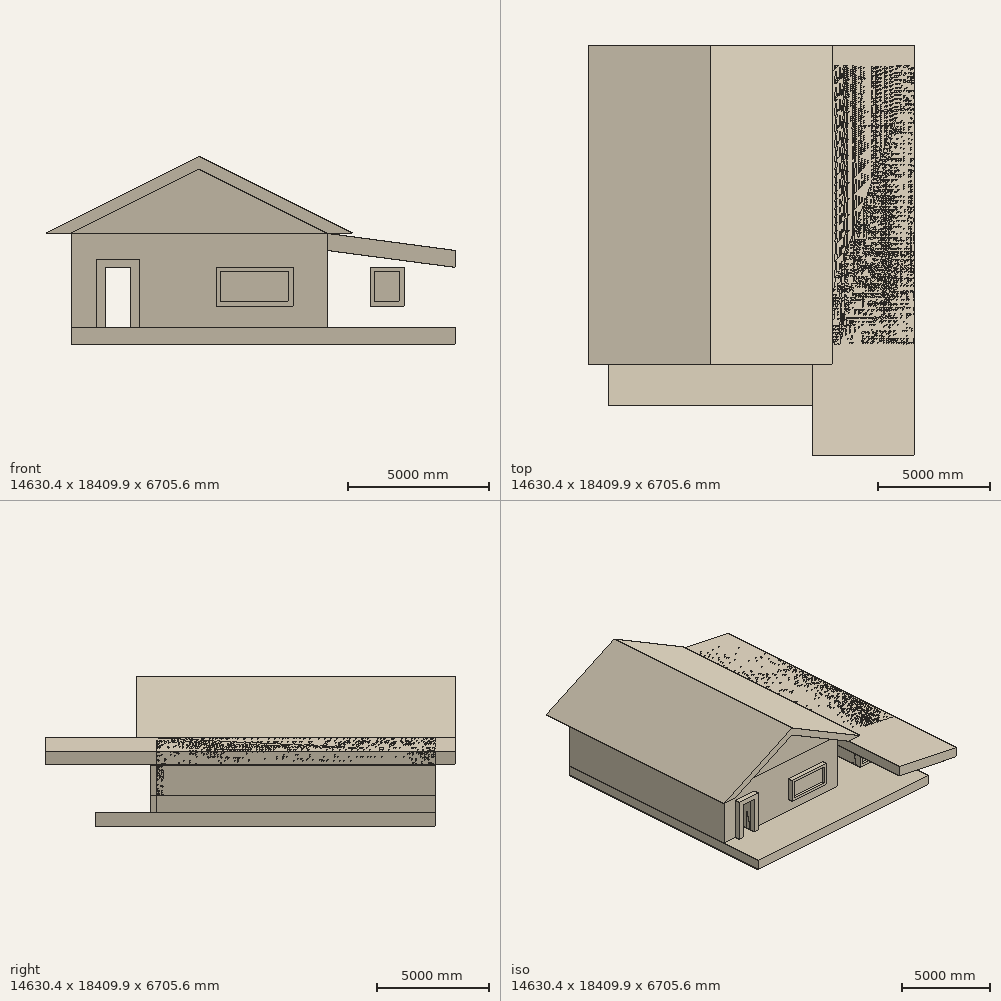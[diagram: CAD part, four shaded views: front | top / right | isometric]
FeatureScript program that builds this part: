
annotation { "Feature Type Name" : "Feature", "Feature Type Description" : "" }
export const myFeature = defineFeature(function(context is Context, id is Id, definition is map)
    precondition{}
    {
        {
            var Q0;
            Q0=qCreatedBy(makeId("Front.planeOp"),FACE);
            var sketch = newSketch(context, id + "F0", { "sketchPlane" : qUnion([Q0])});
            skLineSegment(sketch, "E0", {"start": v(0, 0) * mm, "end": v(-4572, 0) * mm});
            skLineSegment(sketch, "E1", {"start": v(0, 0) * mm, "end": v(4572, 0) * mm});
            skLineSegment(sketch, "E2", {"start": v(0, 0) * mm, "end": v(0, 2286) * mm});
            skLineSegment(sketch, "E3", {"start": v(0, 2286) * mm, "end": v(-4572, 0) * mm});
            skLineSegment(sketch, "E4", {"start": v(0, 2286) * mm, "end": v(4572, 0) * mm});
            skLineSegment(sketch, "E5", {"start": v(-4572, 0) * mm, "end": v(-5486.4, 0) * mm});
            skLineSegment(sketch, "E6", {"start": v(0, 2286) * mm, "end": v(0, 2743.2) * mm});
            skLineSegment(sketch, "E7", {"start": v(0, 2743.2) * mm, "end": v(-5486.4, 0) * mm});
            skLineSegment(sketch, "E8", {"start": v(4572, 0) * mm, "end": v(5486.4, 0) * mm});
            skLineSegment(sketch, "E9", {"start": v(5486.4, 0) * mm, "end": v(0, 2743.2) * mm});
            skLineSegment(sketch, "E10", {"start": v(-4572, 0) * mm, "end": v(-4572, -3352.8) * mm});
            skLineSegment(sketch, "E11", {"start": v(-4572, -3352.8) * mm, "end": v(4572, -3352.8) * mm});
            skLineSegment(sketch, "E12", {"start": v(4572, -3352.8) * mm, "end": v(4572, 0) * mm});
            skLineSegment(sketch, "E13", {"start": v(-4572, -3352.8) * mm, "end": v(-4572, -3962.4) * mm});
            skLineSegment(sketch, "E14", {"start": v(-4572, -3962.4) * mm, "end": v(4572, -3962.4) * mm});
            skLineSegment(sketch, "E15", {"start": v(4572, -3962.4) * mm, "end": v(4572, -3352.8) * mm});
            skLineSegment(sketch, "E16.bottom", {"start": v(-3352.8, -3352.8) * mm, "end": v(-2438.4, -3352.8) * mm});
            skLineSegment(sketch, "E16.top", {"start": v(-3352.8, -1219.2) * mm, "end": v(-2438.4, -1219.2) * mm});
            skLineSegment(sketch, "E16.left", {"start": v(-3352.8, -3352.8) * mm, "end": v(-3352.8, -1219.2) * mm});
            skLineSegment(sketch, "E16.right", {"start": v(-2438.4, -3352.8) * mm, "end": v(-2438.4, -1219.2) * mm});
            skLineSegment(sketch, "E17.bottom", {"start": v(609.6, -1219.2) * mm, "end": v(3352.8, -1219.2) * mm});
            skLineSegment(sketch, "E17.top", {"start": v(609.6, -2590.8) * mm, "end": v(3352.8, -2590.8) * mm});
            skLineSegment(sketch, "E17.left", {"start": v(609.6, -1219.2) * mm, "end": v(609.6, -2590.8) * mm});
            skLineSegment(sketch, "E17.right", {"start": v(3352.8, -1219.2) * mm, "end": v(3352.8, -2590.8) * mm});
            skLineSegment(sketch, "E18", {"start": v(4572, -3962.4) * mm, "end": v(9144, -3962.4) * mm});
            skLineSegment(sketch, "E19", {"start": v(9144, -3962.4) * mm, "end": v(9144, -3352.8) * mm});
            skLineSegment(sketch, "E20", {"start": v(9144, -3352.8) * mm, "end": v(4572, -3352.8) * mm});
            skLineSegment(sketch, "E21", {"start": v(4572, 0) * mm, "end": v(9144, -609.6) * mm});
            skLineSegment(sketch, "E22", {"start": v(9144, -609.6) * mm, "end": v(9144, -3352.8) * mm});
            skLineSegment(sketch, "E23", {"start": v(6096, -2590.8) * mm, "end": v(7315.2, -2590.8) * mm});
            skLineSegment(sketch, "E24", {"start": v(7315.2, -2590.8) * mm, "end": v(7315.2, -1219.2) * mm});
            skLineSegment(sketch, "E25", {"start": v(7315.2, -1219.2) * mm, "end": v(6096, -1219.2) * mm});
            skLineSegment(sketch, "E26", {"start": v(6096, -1219.2) * mm, "end": v(6096, -2590.8) * mm});
            skLineSegment(sketch, "E27.0", {"start": v(762, -1371.6) * mm, "end": v(3200.4, -1371.6) * mm});
            skLineSegment(sketch, "E27.1", {"start": v(762, -1371.6) * mm, "end": v(762, -2438.4) * mm});
            skLineSegment(sketch, "E27.2", {"start": v(762, -2438.4) * mm, "end": v(3200.4, -2438.4) * mm});
            skLineSegment(sketch, "E27.3", {"start": v(3200.4, -1371.6) * mm, "end": v(3200.4, -2438.4) * mm});
            skLineSegment(sketch, "E28", {"start": v(9144, -3352.8) * mm, "end": v(9144, -1213.57) * mm});
            skLineSegment(sketch, "E29", {"start": v(4572, 0) * mm, "end": v(4572, -609.6) * mm});
            skLineSegment(sketch, "E30", {"start": v(4572, -609.6) * mm, "end": v(9144, -1213.57) * mm});
            skLineSegment(sketch, "E31.0", {"start": v(7162.8, -1371.6) * mm, "end": v(6248.4, -1371.6) * mm});
            skLineSegment(sketch, "E31.1", {"start": v(7162.8, -2438.4) * mm, "end": v(7162.8, -1371.6) * mm});
            skLineSegment(sketch, "E31.2", {"start": v(6248.4, -2438.4) * mm, "end": v(7162.8, -2438.4) * mm});
            skLineSegment(sketch, "E31.3", {"start": v(6248.4, -1371.6) * mm, "end": v(6248.4, -2438.4) * mm});
            skLineSegment(sketch, "E32.0", {"start": v(-2133.6, -3352.8) * mm, "end": v(-2133.6, -914.4) * mm});
            skLineSegment(sketch, "E32.1", {"start": v(-3657.6, -914.4) * mm, "end": v(-2133.6, -914.4) * mm});
            skLineSegment(sketch, "E32.2", {"start": v(-3657.6, -3352.8) * mm, "end": v(-3657.6, -914.4) * mm});
            skLineSegment(sketch, "E33", {"start": v(-2133.6, -3352.8) * mm, "end": v(-2438.4, -3352.8) * mm});
            skText(sketch, "E34", { "text": "Property of\nSTEMINEM", "fontName": "OpenSans-Bold.ttf"});
            const initialGuessF0  = {"E34": [-4.71982, 5.77055, 1, 0, 1.2192]};
            skSetInitialGuess(sketch, initialGuessF0);
            skSolve(sketch);
        }
        {
            var Q0;
            Q0=makeQuery(id+"F0.imprint","IMPRINT",FACE,{"disambiguationData":[TD([[makeQuery(id+"F0.imprint","IMPRINT",EDGE,{"derivedFrom":sQuery(id+"F0.wireOp",EDGE,"E3")}),-1.0]])]});
            var Q1;
            Q1=makeQuery(id+"F0.imprint","IMPRINT",FACE,{"disambiguationData":[TD([[makeQuery(id+"F0.imprint","IMPRINT",EDGE,{"derivedFrom":sQuery(id+"F0.wireOp",EDGE,"E4")}),1.0]])]});
            var Q2;
            Q2=makeQuery(id+"F0.imprint","IMPRINT",FACE,{"disambiguationData":[TD([[makeQuery(id+"F0.imprint","IMPRINT",EDGE,{"derivedFrom":sQuery(id+"F0.wireOp",EDGE,"E21")}),-1.0]])]});
            extrude(context, id + "F1", {"entities" : qUnion([Q0, Q1, Q2]), "depth" : 1219.2 * mm, "offsetDistance" : 30.48 * mm, "hasSecondDirection" : true, "secondDirectionOppositeDirection" : true, "secondDirectionDepth" : 13106.4 * mm});
        }
        {
            var Q0;
            Q0=makeQuery(id+"F0.imprint","IMPRINT",FACE,{"disambiguationData":[TD([[makeQuery(id+"F0.imprint","IMPRINT",EDGE,{"derivedFrom":sQuery(id+"F0.wireOp",EDGE,"E0")}),-1.0]])]});
            var Q1;
            Q1=makeQuery(id+"F0.imprint","IMPRINT",FACE,{"disambiguationData":[TD([[makeQuery(id+"F0.imprint","IMPRINT",EDGE,{"derivedFrom":sQuery(id+"F0.wireOp",EDGE,"E1")}),1.0]])]});
            extrude(context, id + "F2", {"entities" : qUnion([Q0, Q1]), "operationType" : NewBodyOperationType.ADD, "depth" : 304.8 * mm, "offsetDistance" : 30.48 * mm, "hasSecondDirection" : true, "secondDirectionOppositeDirection" : true, "secondDirectionDepth" : 12192 * mm});
        }
        {
            var Q0;
            {var subQ0=sQuery(id+"F0.wireOp",EDGE,"E13");Q0=makeQuery(id+"F0.imprint","IMPRINT",FACE,{"disambiguationData":[TD([[makeQuery(id+"F0.imprint","IMPRINT",EDGE,{"derivedFrom":subQ0}),1.0]])]});}
            var Q1;
            Q1=makeQuery(id+"F0.imprint","IMPRINT",FACE,{"disambiguationData":[TD([[makeQuery(id+"F0.imprint","IMPRINT",EDGE,{"derivedFrom":sQuery(id+"F0.wireOp",EDGE,"E15")}),-1.0]])]});
            extrude(context, id + "F3", {"entities" : qUnion([Q0, Q1]), "depth" : 3048 * mm, "offsetDistance" : 30.48 * mm, "hasSecondDirection" : true, "secondDirectionOppositeDirection" : true, "secondDirectionDepth" : 12192 * mm});
        }
        {
            var Q0;
            Q0=makeQuery(id+"F0.imprint","IMPRINT",FACE,{"disambiguationData":[TD([[makeQuery(id+"F0.imprint","IMPRINT",EDGE,{"derivedFrom":sQuery(id+"F0.wireOp",EDGE,"E0")}),1.0]])]});
            var Q1;
            Q1=makeQuery(id+"F0.imprint","IMPRINT",FACE,{"disambiguationData":[TD([[makeQuery(id+"F0.imprint","IMPRINT",EDGE,{"derivedFrom":sQuery(id+"F0.wireOp",EDGE,"E16.bottom")}),1.0]])]});
            var Q2;
            Q2=makeQuery(id+"F0.imprint","IMPRINT",FACE,{"disambiguationData":[TD([[makeQuery(id+"F0.imprint","IMPRINT",EDGE,{"derivedFrom":sQuery(id+"F0.wireOp",EDGE,"E16.top")}),1.0]])]});
            var Q3;
            Q3=makeQuery(id+"F0.imprint","IMPRINT",FACE,{"disambiguationData":[TD([[makeQuery(id+"F0.imprint","IMPRINT",EDGE,{"derivedFrom":sQuery(id+"F0.wireOp",EDGE,"E27.0")}),-1.0]])]});
            var Q4;
            Q4=makeQuery(id+"F0.imprint","IMPRINT",FACE,{"disambiguationData":[TD([[makeQuery(id+"F0.imprint","IMPRINT",EDGE,{"derivedFrom":sQuery(id+"F0.wireOp",EDGE,"E17.bottom")}),-1.0]])]});
            var Q5;
            Q5=makeQuery(id+"F0.imprint","IMPRINT",FACE,{"disambiguationData":[TD([[makeQuery(id+"F0.imprint","IMPRINT",EDGE,{"derivedFrom":sQuery(id+"F0.wireOp",EDGE,"E12")}),-1.0]])]});
            var Q6;
            Q6=makeQuery(id+"F0.imprint","IMPRINT",FACE,{"disambiguationData":[TD([[makeQuery(id+"F0.imprint","IMPRINT",EDGE,{"derivedFrom":sQuery(id+"F0.wireOp",EDGE,"E23")}),1.0]])]});
            var Q7;
            Q7=makeQuery(id+"F0.imprint","IMPRINT",FACE,{"disambiguationData":[TD([[makeQuery(id+"F0.imprint","IMPRINT",EDGE,{"derivedFrom":sQuery(id+"F0.wireOp",EDGE,"E31.0")}),1.0]])]});
            extrude(context, id + "F4", {"entities" : qUnion([Q0, Q1, Q2, Q3, Q4, Q5, Q6, Q7]), "depth" : 304.8 * mm, "offsetDistance" : 30.48 * mm, "hasSecondDirection" : true, "secondDirectionOppositeDirection" : true, "secondDirectionDepth" : 12192 * mm});
        }
        {
            var Q0;
            Q0=makeQuery(id+"F0.imprint","IMPRINT",FACE,{"disambiguationData":[TD([[makeQuery(id+"F0.imprint","IMPRINT",EDGE,{"derivedFrom":sQuery(id+"F0.wireOp",EDGE,"E16.bottom")}),1.0]])]});
            var Q1;
            Q1=makeQuery(id+"F0.imprint","IMPRINT",FACE,{"disambiguationData":[TD([[makeQuery(id+"F0.imprint","IMPRINT",EDGE,{"derivedFrom":sQuery(id+"F0.wireOp",EDGE,"E27.0")}),-1.0]])]});
            var Q2;
            Q2=makeQuery(id+"F0.imprint","IMPRINT",FACE,{"disambiguationData":[TD([[makeQuery(id+"F0.imprint","IMPRINT",EDGE,{"derivedFrom":sQuery(id+"F0.wireOp",EDGE,"E31.0")}),1.0]])]});
            extrude(context, id + "F5", {"entities" : qUnion([Q0, Q1, Q2]), "depth" : 457.2 * mm, "offsetDistance" : 30.48 * mm});
        }
        {
            var Q0;
            Q0=makeQuery(id+"F0.imprint","IMPRINT",FACE,{"disambiguationData":[TD([[makeQuery(id+"F0.imprint","IMPRINT",EDGE,{"derivedFrom":sQuery(id+"F0.wireOp",EDGE,"E16.top")}),1.0]])]});
            var Q1;
            Q1=makeQuery(id+"F0.imprint","IMPRINT",FACE,{"disambiguationData":[TD([[makeQuery(id+"F0.imprint","IMPRINT",EDGE,{"derivedFrom":sQuery(id+"F0.wireOp",EDGE,"E17.bottom")}),-1.0]])]});
            var Q2;
            Q2=makeQuery(id+"F0.imprint","IMPRINT",FACE,{"disambiguationData":[TD([[makeQuery(id+"F0.imprint","IMPRINT",EDGE,{"derivedFrom":sQuery(id+"F0.wireOp",EDGE,"E23")}),1.0]])]});
            extrude(context, id + "F6", {"entities" : qUnion([Q0, Q1, Q2]), "depth" : 609.6 * mm, "offsetDistance" : 30.48 * mm});
        }
        {
            var Q0;
            Q0=makeQuery(id+"F1.opExtrude","CAP_FACE",FACE,{"disambiguationData":[OSD([sQuery(id+"F0.wireOp",EDGE,"E21"),sQuery(id+"F0.wireOp",EDGE,"E22"),sQuery(id+"F0.wireOp",EDGE,"E29"),sQuery(id+"F0.wireOp",EDGE,"E30")])],"isStart":false});
            extrude(context, id + "F7", {"entities" : qUnion([Q0]), "operationType" : NewBodyOperationType.ADD, "depth" : 4084.32 * mm, "offsetDistance" : 30.48 * mm, "hasSecondDirection" : true, "secondDirectionOppositeDirection" : true, "secondDirectionDepth" : 30.48 * mm});
        }
    });
